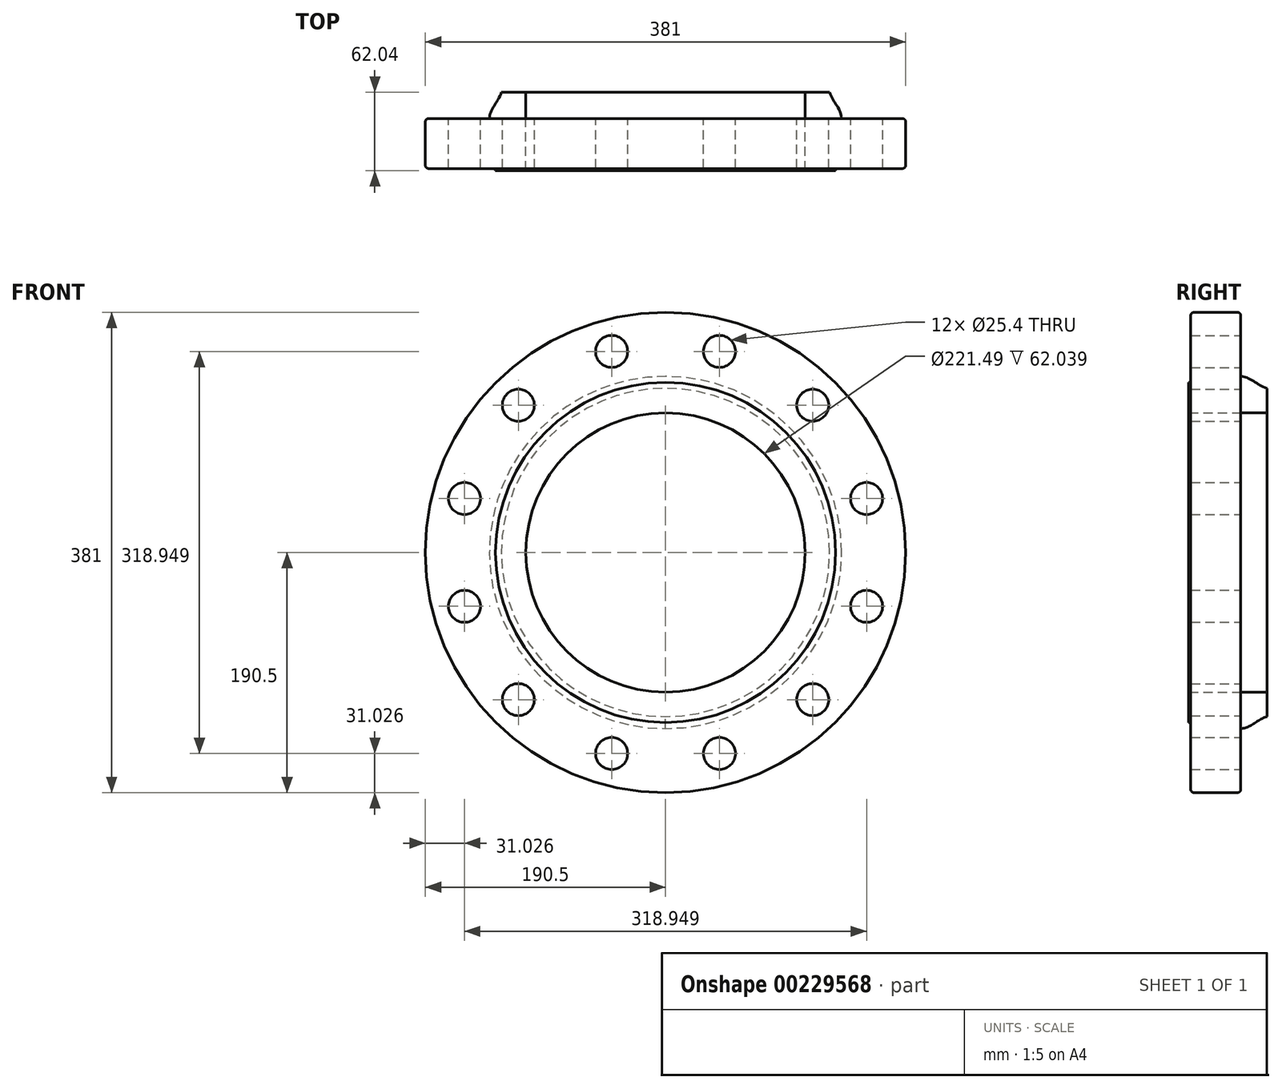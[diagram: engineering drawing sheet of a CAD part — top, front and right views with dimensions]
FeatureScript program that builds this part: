
annotation { "Feature Type Name" : "Feature", "Feature Type Description" : "" }
export const myFeature = defineFeature(function(context is Context, id is Id, definition is map)
    precondition{}
    {
        {
            var Q0;
            Q0=qCreatedBy(makeId("Front.planeOp"),FACE);
            var sketch = newSketch(context, id + "F0", { "sketchPlane" : qUnion([Q0])});
            skCircle(sketch, "E0", {"center": v(0, 0) * mm, "radius": 190.5 * mm});
            skCircle(sketch, "E1", {"center": v(0, 0) * mm, "radius": 110.74 * mm});
            skCircle(sketch, "E2", {"center": v(42.73, 159.47) * mm, "radius": 12.7 * mm});
            skCircle(sketch, "E3.1.0", {"center": v(-42.73, 159.47) * mm, "radius": 12.7 * mm});
            skCircle(sketch, "E3.2.0", {"center": v(-116.74, 116.74) * mm, "radius": 12.7 * mm});
            skCircle(sketch, "E3.3.0", {"center": v(-159.47, 42.73) * mm, "radius": 12.7 * mm});
            skCircle(sketch, "E3.4.0", {"center": v(-159.47, -42.73) * mm, "radius": 12.7 * mm});
            skCircle(sketch, "E3.5.0", {"center": v(-116.74, -116.74) * mm, "radius": 12.7 * mm});
            skCircle(sketch, "E3.6.0", {"center": v(-42.73, -159.47) * mm, "radius": 12.7 * mm});
            skCircle(sketch, "E3.7.0", {"center": v(42.73, -159.47) * mm, "radius": 12.7 * mm});
            skCircle(sketch, "E3.8.0", {"center": v(116.74, -116.74) * mm, "radius": 12.7 * mm});
            skCircle(sketch, "E3.9.0", {"center": v(159.47, -42.73) * mm, "radius": 12.7 * mm});
            skCircle(sketch, "E3.10.0", {"center": v(159.47, 42.73) * mm, "radius": 12.7 * mm});
            skCircle(sketch, "E3.11.0", {"center": v(116.74, 116.74) * mm, "radius": 12.7 * mm});
            skSolve(sketch);
        }
        {
            var Q0;
            Q0 = qSketchRegion(id + "F0", true);
            extrude(context, id + "F1", {"entities" : qUnion([Q0]), "depth" : 39.62 * mm});
        }
        {
            var Q0;
            Q0=makeQuery(id+"F1.opExtrude","CAP_FACE",FACE,{"disambiguationData":[OSD([sQuery(id+"F0.wireOp",EDGE,"E0"),sQuery(id+"F0.wireOp",EDGE,"E1"),sQuery(id+"F0.wireOp",EDGE,"E2"),sQuery(id+"F0.wireOp",EDGE,"E3.1.0"),sQuery(id+"F0.wireOp",EDGE,"E3.2.0"),sQuery(id+"F0.wireOp",EDGE,"E3.3.0"),sQuery(id+"F0.wireOp",EDGE,"E3.4.0"),sQuery(id+"F0.wireOp",EDGE,"E3.5.0"),sQuery(id+"F0.wireOp",EDGE,"E3.6.0"),sQuery(id+"F0.wireOp",EDGE,"E3.7.0"),sQuery(id+"F0.wireOp",EDGE,"E3.8.0"),sQuery(id+"F0.wireOp",EDGE,"E3.9.0"),sQuery(id+"F0.wireOp",EDGE,"E3.10.0"),sQuery(id+"F0.wireOp",EDGE,"E3.11.0")])],"isStart":false});
            var sketch = newSketch(context, id + "F2", { "sketchPlane" : qUnion([Q0])});
            skCircle(sketch, "E4", {"center": v(0, 0) * mm, "radius": 134.87 * mm});
            skCircle(sketch, "E5", {"center": v(0, 0) * mm, "radius": 110.74 * mm});
            skSolve(sketch);
        }
        {
            var Q0;
            Q0 = qSketchRegion(id + "F2", true);
            extrude(context, id + "F3", {"entities" : qUnion([Q0]), "operationType" : NewBodyOperationType.ADD, "depth" : 1.59 * mm});
        }
        {
            var Q0;
            Q0=qCreatedBy(makeId("Right.planeOp"),FACE);
            var sketch = newSketch(context, id + "F4", { "sketchPlane" : qUnion([Q0])});
            skLineSegment(sketch, "E6", {"start": v(0, 0) * mm, "end": v(20.83, 0) * mm});
            skLineSegment(sketch, "E7", {"start": v(20.83, 110.74) * mm, "end": v(20.83, 130.18) * mm});
            skLineSegment(sketch, "E8", {"start": v(20.83, 110.74) * mm, "end": v(0, 110.74) * mm});
            skLineSegment(sketch, "E9", {"start": v(0, 110.74) * mm, "end": v(0, 130.18) * mm});
            skLineSegment(sketch, "E10", {"start": v(0, 130.18) * mm, "end": v(0, 139.7) * mm});
            skFitSpline(sketch, "E11", {"points": [v(0, 139.7) * mm, v(20.83, 130.18) * mm], "startDerivative": vector(23.38, -0.6) * mm, "endDerivative": vector(23.5, -7.1) * mm});
            skSolve(sketch);
        }
        {
            var Q0;
            Q0 = qSketchRegion(id + "F4", true);
            var Q1;
            Q1=sQuery(id+"F4.wireOp",EDGE,"E6");
            revolve(context, id + "F5", {"operationType" : NewBodyOperationType.ADD, "entities" : qUnion([Q0]), "axis" : qUnion([Q1]), "revolveType" : RevolveType.FULL});
        }
        {
            var Q0;
            Q0=makeQuery(id+"F1.opExtrude","CAP_EDGE",EDGE,{"disambiguationData":[OSD([sQuery(id+"F0.wireOp",EDGE,"E0")])],"isStart":true});
            var Q1;
            Q1=makeQuery(id+"F1.opExtrude","CAP_EDGE",EDGE,{"disambiguationData":[OSD([sQuery(id+"F0.wireOp",EDGE,"E0")])],"isStart":false});
            var Q2;
            Q2=makeQuery(id+"F5.opRevolve","SWEPT_EDGE",EDGE,{"disambiguationData":[OSD([sQuery(id+"F4.wireOp",EDGE,"E10"),sQuery(id+"F4.wireOp",EDGE,"E11")])]});
            fillet(context, id + "F6", {"entities" : qUnion([Q0, Q1, Q2]), "radius" : 2.54 * mm, "tangentPropagation" : true, "allowEdgeOverflow" : false});
        }
    });
